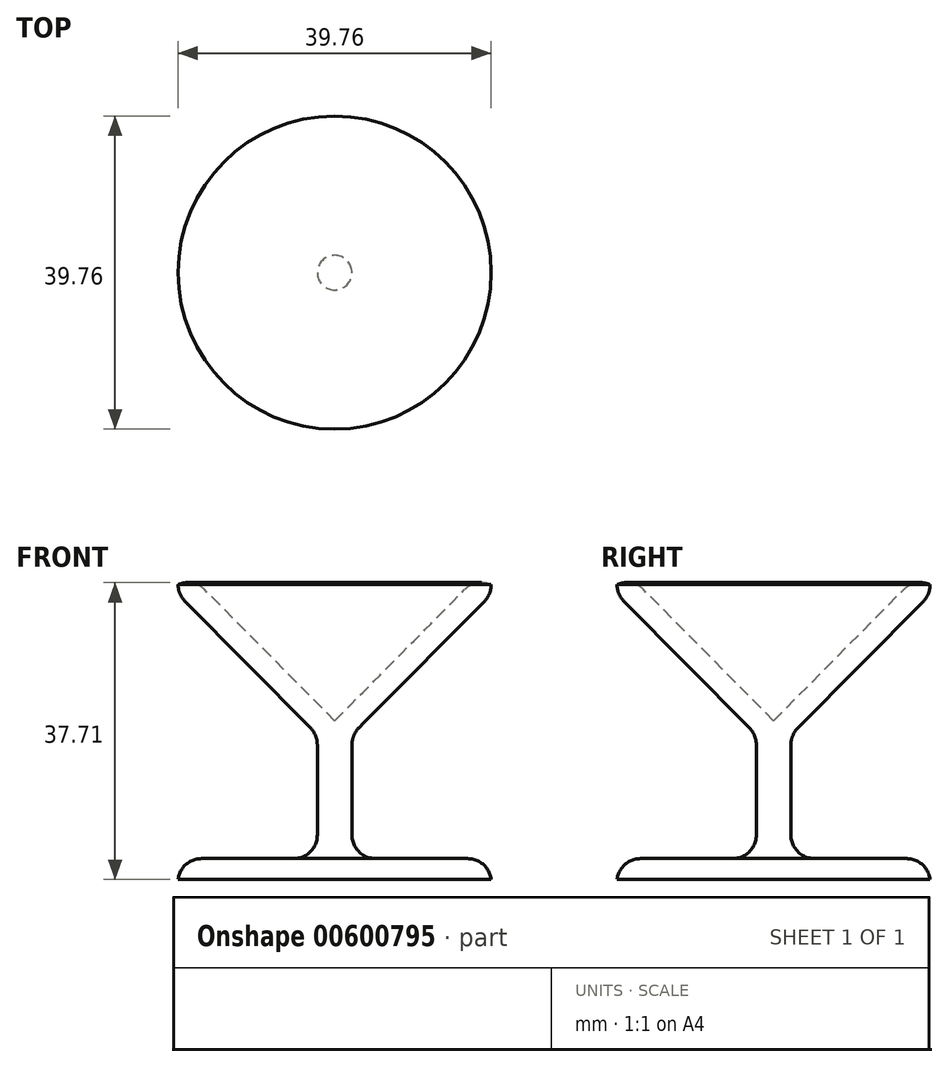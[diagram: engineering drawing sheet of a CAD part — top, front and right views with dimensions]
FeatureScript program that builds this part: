
annotation { "Feature Type Name" : "Feature", "Feature Type Description" : "" }
export const myFeature = defineFeature(function(context is Context, id is Id, definition is map)
    precondition{}
    {
        {
            var Q0;
            Q0=qCreatedBy(makeId("Front.planeOp"),FACE);
            var sketch = newSketch(context, id + "F0", { "sketchPlane" : qUnion([Q0])});
            skLineSegment(sketch, "E0", {"start": v(0, 0) * mm, "end": v(19.88, 0) * mm});
            skLineSegment(sketch, "E1", {"start": v(19.88, 0) * mm, "end": v(19.88, 2.64) * mm});
            skLineSegment(sketch, "E2", {"start": v(19.88, 2.64) * mm, "end": v(0, 2.64) * mm});
            skLineSegment(sketch, "E3", {"start": v(0, 2.64) * mm, "end": v(0, 20.15) * mm});
            skLineSegment(sketch, "E4", {"start": v(0, 20.15) * mm, "end": v(19.88, 40.2) * mm});
            skLineSegment(sketch, "E5", {"start": v(19.88, 36.2) * mm, "end": v(19.88, 40.2) * mm});
            skLineSegment(sketch, "E6", {"start": v(19.88, 36.2) * mm, "end": v(0, 16.14) * mm});
            skLineSegment(sketch, "E7", {"start": v(0, 0) * mm, "end": v(0, 2.64) * mm});
            skLineSegment(sketch, "E8", {"start": v(2.2, 2.64) * mm, "end": v(2.2, 18.37) * mm});
            skSolve(sketch);
        }
        {
            var Q0;
            {var subQ3=sQuery(id+"F0.wireOp",EDGE,"E4");Q0=makeQuery(id+"F0.imprint","IMPRINT",FACE,{"disambiguationData":[TD([[makeQuery(id+"F0.imprint","IMPRINT",EDGE,{"derivedFrom":subQ3}),-1.0]])]});}
            var Q1;
            Q1=makeQuery(id+"F0.imprint","IMPRINT",FACE,{"disambiguationData":[TD([[makeQuery(id+"F0.imprint","IMPRINT",EDGE,{"derivedFrom":sQuery(id+"F0.wireOp",EDGE,"E0")}),1.0]])]});
            var Q2;
            {var subQ3=sQuery(id+"F0.wireOp",EDGE,"E8");Q2=makeQuery(id+"F0.imprint","IMPRINT",FACE,{"disambiguationData":[TD([[makeQuery(id+"F0.imprint","IMPRINT",EDGE,{"derivedFrom":subQ3}),1.0]])]});}
            var Q3;
            Q3=sQuery(id+"F0.wireOp",EDGE,"E3");
            revolve(context, id + "F1", {"entities" : qUnion([Q0, Q1, Q2]), "axis" : qUnion([Q3]), "revolveType" : RevolveType.FULL});
        }
        {
            var Q0;
            Q0=makeQuery(id+"F1.opRevolve","SWEPT_EDGE",EDGE,{"disambiguationData":[OSD([sQuery(id+"F0.wireOp",EDGE,"E5"),sQuery(id+"F0.wireOp",EDGE,"E6")])]});
            var Q1;
            Q1=makeQuery(id+"F1.opRevolve","SWEPT_EDGE",EDGE,{"disambiguationData":[OSD([sQuery(id+"F0.wireOp",EDGE,"E6"),sQuery(id+"F0.wireOp",EDGE,"E8")])]});
            var Q2;
            Q2=makeQuery(id+"F1.opRevolve","SWEPT_EDGE",EDGE,{"disambiguationData":[OSD([sQuery(id+"F0.wireOp",EDGE,"E1"),sQuery(id+"F0.wireOp",EDGE,"E2")])]});
            fillet(context, id + "F2", {"entities" : qUnion([Q0, Q1, Q2]), "radius" : 3 * mm, "tangentPropagation" : true, "allowEdgeOverflow" : false});
        }
        {
            var Q0;
            Q0=makeQuery(id+"F1.opRevolve","SWEPT_EDGE",EDGE,{"disambiguationData":[OSD([sQuery(id+"F0.wireOp",EDGE,"E2"),sQuery(id+"F0.wireOp",EDGE,"E8")])]});
            var Q1;
            Q1=makeQuery(id+"F1.opRevolve","SWEPT_EDGE",EDGE,{"disambiguationData":[OSD([sQuery(id+"F0.wireOp",EDGE,"E4"),sQuery(id+"F0.wireOp",EDGE,"E5")])]});
            fillet(context, id + "F3", {"entities" : qUnion([Q0, Q1]), "radius" : 3 * mm, "tangentPropagation" : true, "allowEdgeOverflow" : false});
        }
    });
